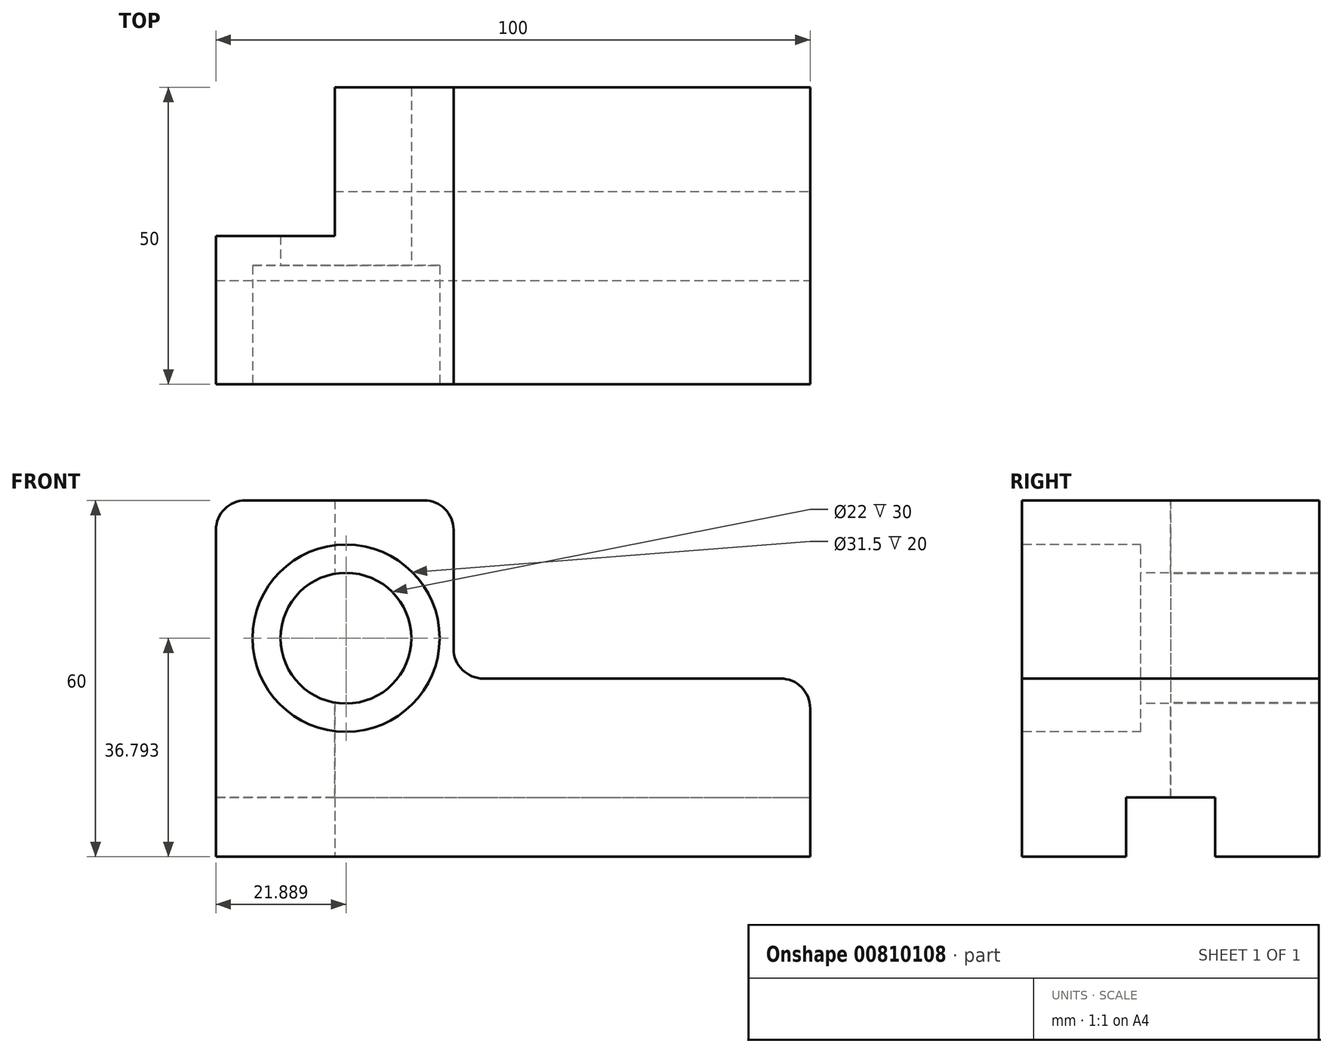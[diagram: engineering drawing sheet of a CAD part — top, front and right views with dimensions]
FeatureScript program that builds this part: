
annotation { "Feature Type Name" : "Feature", "Feature Type Description" : "" }
export const myFeature = defineFeature(function(context is Context, id is Id, definition is map)
    precondition{}
    {
        {
            var Q0;
            Q0=qCreatedBy(makeId("Front.planeOp"),FACE);
            var sketch = newSketch(context, id + "F0", { "sketchPlane" : qUnion([Q0])});
            skLineSegment(sketch, "E0.bottom", {"start": v(-100, 60) * mm, "end": v(-60, 60) * mm});
            skLineSegment(sketch, "E0.top", {"start": v(-100, 0) * mm, "end": v(-60, 0) * mm});
            skLineSegment(sketch, "E0.left", {"start": v(-100, 60) * mm, "end": v(-100, 0) * mm});
            skLineSegment(sketch, "E0.right", {"start": v(-60, 60) * mm, "end": v(-60, 0) * mm});
            skLineSegment(sketch, "E1.bottom", {"start": v(-60, 0) * mm, "end": v(0, 0) * mm});
            skLineSegment(sketch, "E1.top", {"start": v(-60, 30) * mm, "end": v(0, 30) * mm});
            skLineSegment(sketch, "E1.left", {"start": v(-60, 0) * mm, "end": v(-60, 30) * mm});
            skLineSegment(sketch, "E1.right", {"start": v(0, 0) * mm, "end": v(0, 30) * mm});
            skSolve(sketch);
        }
        {
            var Q0;
            Q0=makeQuery(id+"F0.imprint","IMPRINT",FACE,{"disambiguationData":[TD([[makeQuery(id+"F0.imprint","IMPRINT",EDGE,{"derivedFrom":sQuery(id+"F0.wireOp",EDGE,"E0.bottom")}),-1.0]])]});
            var Q1;
            Q1=makeQuery(id+"F0.imprint","IMPRINT",FACE,{"disambiguationData":[TD([[makeQuery(id+"F0.imprint","IMPRINT",EDGE,{"derivedFrom":sQuery(id+"F0.wireOp",EDGE,"E1.bottom")}),1.0]])]});
            extrude(context, id + "F1", {"entities" : qUnion([Q0, Q1]), "endBound" : BoundingType.SYMMETRIC, "depth" : 50 * mm, "offsetDistance" : 25 * mm});
        }
        {
            var Q0;
            Q0=makeQuery(id+"F1.opExtrude","SWEPT_EDGE",EDGE,{"disambiguationData":[OSD([sQuery(id+"F0.wireOp",EDGE,"E0.right"),sQuery(id+"F0.wireOp",EDGE,"E1.top"),sQuery(id+"F0.wireOp",EDGE,"E1.left")])]});
            var Q1;
            Q1=makeQuery(id+"F1.opExtrude","SWEPT_EDGE",EDGE,{"disambiguationData":[OSD([sQuery(id+"F0.wireOp",EDGE,"E0.bottom"),sQuery(id+"F0.wireOp",EDGE,"E0.right")])]});
            var Q2;
            Q2=makeQuery(id+"F1.opExtrude","SWEPT_EDGE",EDGE,{"disambiguationData":[OSD([sQuery(id+"F0.wireOp",EDGE,"E1.top"),sQuery(id+"F0.wireOp",EDGE,"E1.right")])]});
            var Q3;
            Q3=makeQuery(id+"F1.opExtrude","SWEPT_EDGE",EDGE,{"disambiguationData":[OSD([sQuery(id+"F0.wireOp",EDGE,"E0.bottom"),sQuery(id+"F0.wireOp",EDGE,"E0.left")])]});
            fillet(context, id + "F2", {"entities" : qUnion([Q0, Q1, Q2, Q3]), "radius" : 5 * mm, "tangentPropagation" : true, "allowEdgeOverflow" : false});
        }
        {
            var Q0;
            Q0=makeQuery(id+"F1.opExtrude","CAP_FACE",FACE,{"disambiguationData":[OSD([sQuery(id+"F0.wireOp",EDGE,"E0.bottom"),sQuery(id+"F0.wireOp",EDGE,"E0.top"),sQuery(id+"F0.wireOp",EDGE,"E0.left"),sQuery(id+"F0.wireOp",EDGE,"E0.right"),sQuery(id+"F0.wireOp",EDGE,"E1.bottom"),sQuery(id+"F0.wireOp",EDGE,"E1.top"),sQuery(id+"F0.wireOp",EDGE,"E1.right")])],"isStart":false});
            var sketch = newSketch(context, id + "F3", { "sketchPlane" : qUnion([Q0])});
            skCircle(sketch, "E2", {"center": v(-78.11, 36.8) * mm, "radius": 8.95 * mm});
            skSolve(sketch);
        }
        {
            var Q0;
            Q0=sQuery(id+"F3.wireOp",VERTEX,"E2.center");
            var Q1;
            Q1=makeQuery(id+"F1.opExtrude","SWEPT_BODY",BODY,{"disambiguationData":[OSD([sQuery(id+"F0.wireOp",EDGE,"E0.bottom"),sQuery(id+"F0.wireOp",EDGE,"E0.top"),sQuery(id+"F0.wireOp",EDGE,"E0.left"),sQuery(id+"F0.wireOp",EDGE,"E0.right"),sQuery(id+"F0.wireOp",EDGE,"E1.bottom"),sQuery(id+"F0.wireOp",EDGE,"E1.top"),sQuery(id+"F0.wireOp",EDGE,"E1.right")])]});
            hole(context, id + "F4", {"style" : HoleStyle.C_BORE, "endStyle" : HoleEndStyle.THROUGH, "standardTappedOrClearance" : lookupTablePath({ "standard" : "ISO", "fit" : "Normal", "size" : "M20", "type" : "Clearance" }), "standardBlindInLast" : lookupTablePath({ "fit" : "Standard", "standard" : "ISO", "size" : "M20", "type" : "Clearance" }), "holeDiameter" : 22 * mm, "cBoreDiameter" : 31.5 * mm, "cBoreDepth" : 20 * mm, "majorDiameter" : 5 * mm, "isTappedThrough" : true, "tappedDepth" : 12 * mm, "tapClearance" : 3, "startFromSketch" : true, "locations" : qUnion([Q0]), "scope" : qUnion([Q1])});
        }
        {
            var Q0;
            Q0=makeQuery(id+"F1.opExtrude","SWEPT_FACE",FACE,{"disambiguationData":[OSD([sQuery(id+"F0.wireOp",EDGE,"E1.right")])]});
            var sketch = newSketch(context, id + "F5", { "sketchPlane" : qUnion([Q0])});
            skLineSegment(sketch, "E3.bottom", {"start": v(-7.5, 10) * mm, "end": v(7.5, 10) * mm});
            skLineSegment(sketch, "E3.top", {"start": v(-7.5, -10) * mm, "end": v(7.5, -10) * mm});
            skLineSegment(sketch, "E3.left", {"start": v(-7.5, 10) * mm, "end": v(-7.5, -10) * mm});
            skLineSegment(sketch, "E3.right", {"start": v(7.5, 10) * mm, "end": v(7.5, -10) * mm});
            skPoint(sketch, "E3.middle", {"position": v(0, 0) * mm});
            skSolve(sketch);
        }
        {
            var Q0;
            {var subQ0=sQuery(id+"F5.wireOp",EDGE,"E3.bottom");Q0=makeQuery(id+"F5.imprint","IMPRINT",FACE,{"disambiguationData":[TD([[makeQuery(id+"F5.imprint","IMPRINT",EDGE,{"derivedFrom":subQ0}),-1.0]])]});}
            extrude(context, id + "F6", {"entities" : qUnion([Q0]), "operationType" : NewBodyOperationType.REMOVE, "endBound" : BoundingType.THROUGH_ALL, "oppositeDirection" : true, "depth" : 25 * mm, "offsetDistance" : 25 * mm});
        }
        {
            var Q0;
            Q0=makeQuery(id+"F1.opExtrude","SWEPT_FACE",FACE,{"disambiguationData":[OSD([sQuery(id+"F0.wireOp",EDGE,"E0.bottom")])]});
            var sketch = newSketch(context, id + "F7", { "sketchPlane" : qUnion([Q0])});
            skPoint(sketch, "E4.oppositeSnap0", {"position": v(-65, 0) * mm});
            skPoint(sketch, "E4.oppositeSnap1", {"position": v(-80, 25) * mm});
            skLineSegment(sketch, "E4.bottom", {"start": v(-123.86, 47.3) * mm, "end": v(-80, 47.3) * mm});
            skLineSegment(sketch, "E4.top", {"start": v(-123.86, 0) * mm, "end": v(-80, 0) * mm});
            skLineSegment(sketch, "E4.left", {"start": v(-123.86, 47.3) * mm, "end": v(-123.86, 0) * mm});
            skLineSegment(sketch, "E4.right", {"start": v(-80, 47.3) * mm, "end": v(-80, 0) * mm});
            skSolve(sketch);
        }
        {
            var Q0;
            {var subQ1=sQuery(id+"F7.wireOp",EDGE,"E4.bottom");Q0=makeQuery(id+"F7.imprint","IMPRINT",FACE,{"disambiguationData":[TD([[makeQuery(id+"F7.imprint","IMPRINT",EDGE,{"derivedFrom":subQ1}),-1.0]])]});}
            var Q1;
            {var subQ0=sQuery(id+"F7.wireOp",EDGE,"E4.right");var subQ1=sQuery(id+"F7.wireOp",EDGE,"E4.top");var subQ2=makeQuery(id+"F7.imprint","INTERSECT",VERTEX,{"derivedFrom":[subQ1,subQ0]});Q1=makeQuery(id+"F7.imprint","IMPRINT",FACE,{"disambiguationData":[TD([[makeQuery(id+"F7.imprint","IMPRINT",EDGE,{"disambiguationData":[TD([[subQ2,1.0]])],"derivedFrom":subQ0}),-1.0]])]});}
            extrude(context, id + "F8", {"entities" : qUnion([Q0, Q1]), "operationType" : NewBodyOperationType.REMOVE, "endBound" : BoundingType.THROUGH_ALL, "oppositeDirection" : true, "depth" : 25 * mm, "offsetDistance" : 25 * mm});
        }
    });
